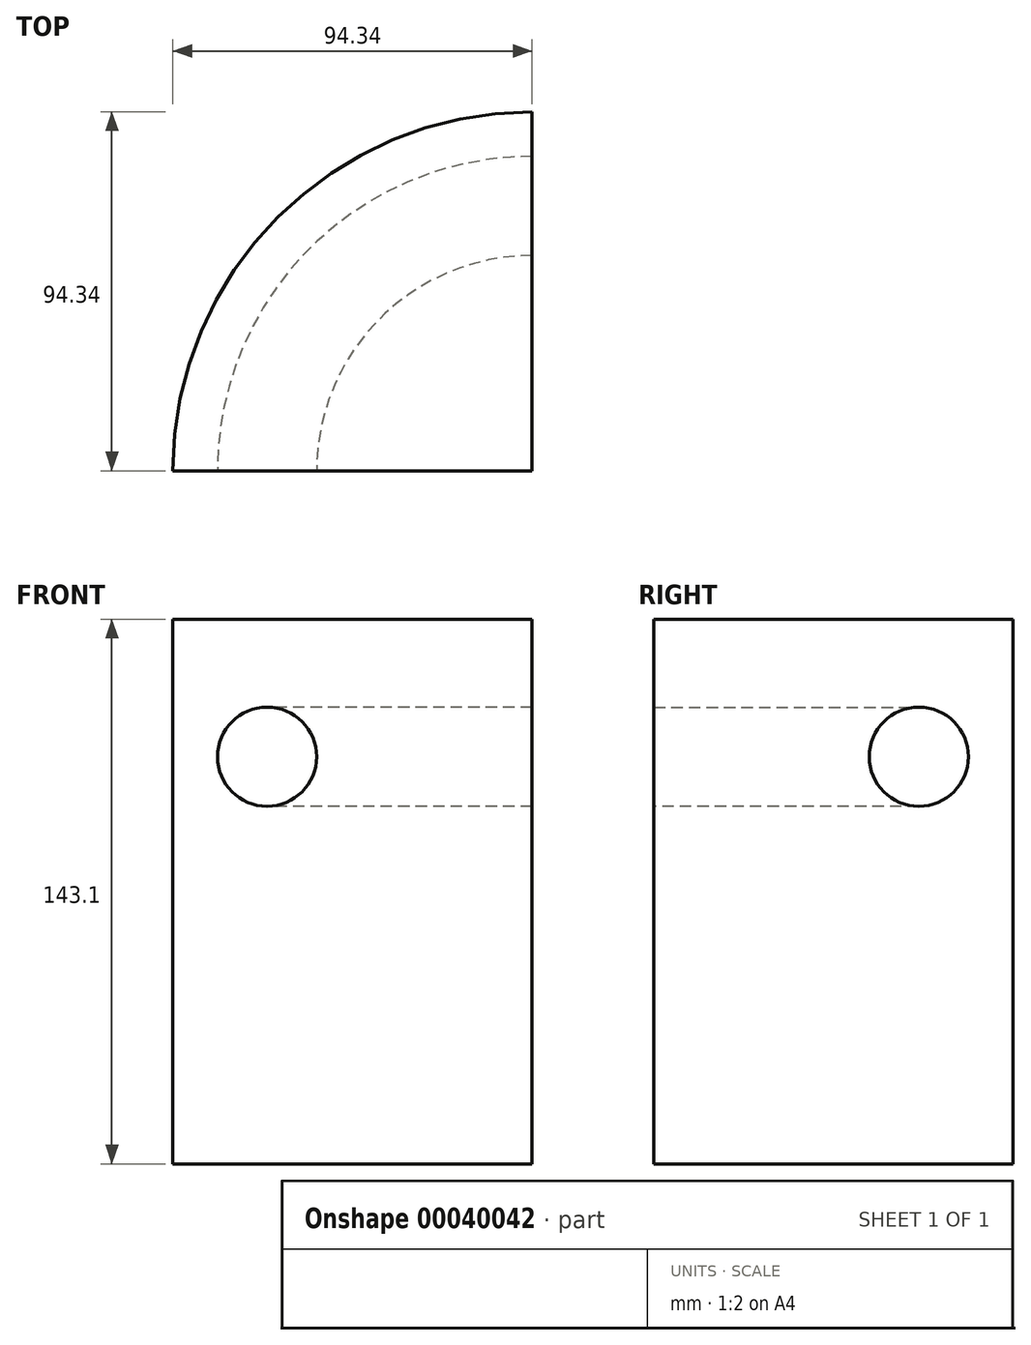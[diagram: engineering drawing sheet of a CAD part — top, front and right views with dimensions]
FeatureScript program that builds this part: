
annotation { "Feature Type Name" : "Feature", "Feature Type Description" : "" }
export const myFeature = defineFeature(function(context is Context, id is Id, definition is map)
    precondition{}
    {
        {
            var Q0;
            Q0=qCreatedBy(makeId("Front.planeOp"),FACE);
            var sketch = newSketch(context, id + "F0", { "sketchPlane" : qUnion([Q0])});
            skLineSegment(sketch, "E0.rect.bottom", {"start": v(47.17, 71.55) * mm, "end": v(-47.17, 71.55) * mm});
            skLineSegment(sketch, "E0.rect.top", {"start": v(47.17, -71.55) * mm, "end": v(-47.17, -71.55) * mm});
            skLineSegment(sketch, "E0.rect.left", {"start": v(47.17, 71.55) * mm, "end": v(47.17, -71.55) * mm});
            skLineSegment(sketch, "E0.rect.right", {"start": v(-47.17, 71.55) * mm, "end": v(-47.17, -71.55) * mm});
            skPoint(sketch, "E0.rect.middle", {"position": v(0, 0) * mm});
            skCircle(sketch, "E1", {"center": v(-22.44, 35.43) * mm, "radius": 13.02 * mm});
            skSolve(sketch);
        }
        {
            var Q0;
            Q0=makeQuery(id+"F0.imprint","IMPRINT",FACE,{"disambiguationData":[TD([[makeQuery(id+"F0.imprint","IMPRINT",EDGE,{"derivedFrom":sQuery(id+"F0.wireOp",EDGE,"E0.rect.bottom")}),1.0]])]});
            var Q1;
            Q1=sQuery(id+"F0.wireOp",EDGE,"E0.rect.left");
            revolve(context, id + "F1", {"entities" : qUnion([Q0]), "axis" : qUnion([Q1]), "revolveType" : RevolveType.ONE_DIRECTION, "angle" : 90 * degree});
        }
    });
